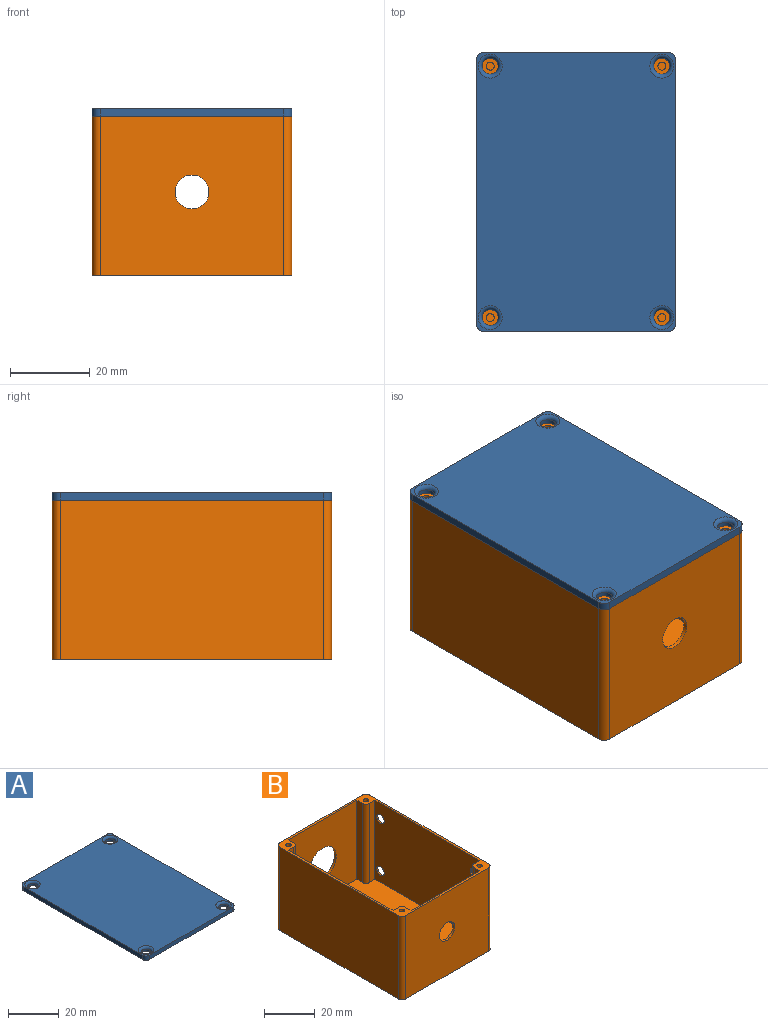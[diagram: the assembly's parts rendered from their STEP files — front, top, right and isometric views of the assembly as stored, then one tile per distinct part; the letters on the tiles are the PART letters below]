
ASSEMBLY  parts=2 mates=1
PART A: 18 faces, bbox 50x70x2 mm
  f0: plane 66x2mm, normal (-1,0,0), area 132mm2, adj f4,f5,f14,f17
  f1: plane 46x2mm, normal (0,-1,0), area 92mm2, adj f4,f5,f14,f15
  f2: plane 66x2mm, normal (1,0,0), area 132mm2, adj f4,f5,f15,f16
  f3: plane 46x2mm, normal (0,1,0), area 92mm2, adj f4,f5,f16,f17
  f4: plane 70x50mm, normal (0,0,1), area 3383.5mm2, adj f0,f1,f2,f3,f10,f11,f12,f13
  f5: plane 70x50mm, normal (0,0,-1), area 3446.3mm2, adj f0,f1,f2,f3,f6,f7,f8,f9
  f6: cylinder r=2mm len=4mm, axis (0,0,1), area 12.6mm2, adj f5,f13
  f7: cylinder r=2mm len=4mm, axis (0,0,1), area 12.6mm2, adj f5,f12
  f8: cylinder r=2mm len=4mm, axis (0,0,1), area 12.6mm2, adj f5,f11
  f9: cylinder r=2mm len=4mm, axis (0,0,1), area 12.6mm2, adj f5,f10
  f10: torus R=3mm, axis (0,0,1), area 23.3mm2, adj f4,f9
  f11: torus R=3mm, axis (0,0,1), area 23.3mm2, adj f4,f8
  f12: torus R=3mm, axis (0,0,1), area 23.3mm2, adj f4,f7
  f13: torus R=3mm, axis (0,0,1), area 23.3mm2, adj f4,f6
  f14: cylinder r=2mm len=2mm, axis (0,0,-1), area 6.3mm2, adj f0,f1,f4,f5
  f15: cylinder r=2mm len=2mm, axis (0,0,1), area 6.3mm2, adj f1,f2,f4,f5
  f16: cylinder r=2mm len=2mm, axis (0,0,-1), area 6.3mm2, adj f2,f3,f4,f5
  f17: cylinder r=2mm len=2mm, axis (0,0,1), area 6.3mm2, adj f0,f3,f4,f5
PART B: 42 faces, bbox 50x70x40 mm
  f0: plane 68x48mm, normal (0,0,1), area 3167.4mm2, adj f1,f2,f3,f4,f11,f12,f13,f14
  f1: plane 58x38mm, normal (-1,0,0), area 2146.2mm2, adj f0,f9,f16,f18,f35,f36,f37,f38
  f2: plane 38x38mm, normal (0,1,0), area 1387.3mm2, adj f0,f9,f13,f15,f40
  f3: plane 58x38mm, normal (1,0,0), area 2204mm2, adj f0,f9,f12,f14
  f4: plane 38x38mm, normal (0,-1,0), area 1267.3mm2, adj f0,f9,f11,f17,f41
  f5: plane 66x40mm, normal (-1,0,0), area 2640mm2, adj f9,f10,f31,f34
  f6: plane 46x40mm, normal (0,-1,0), area 1783.3mm2, adj f9,f10,f31,f32,f40
  f7: plane 66x40mm, normal (1,0,0), area 2558.3mm2, adj f9,f10,f32,f33,f35,f36,f37,f38
  f8: plane 46x40mm, normal (0,1,0), area 1663.3mm2, adj f9,f10,f33,f34,f41
  f9: plane 70x50mm, normal (0,0,1), area 316.6mm2, adj f1,f2,f3,f4,f5,f6,f7,f8
  f10: plane 70x50mm, normal (0,0,-1), area 3496.6mm2, adj f5,f6,f7,f8,f31,f32,f33,f34
  f11: plane 38x3mm, normal (1,0,0), area 114mm2, adj f0,f4,f9,f30
  f12: plane 38x3mm, normal (0,-1,0), area 114mm2, adj f0,f3,f9,f30
  f13: plane 38x3mm, normal (1,0,0), area 114mm2, adj f0,f2,f9,f27
  f14: plane 38x3mm, normal (0,1,0), area 114mm2, adj f0,f3,f9,f27
  f15: plane 38x3mm, normal (-1,0,0), area 114mm2, adj f0,f2,f9,f28
  f16: plane 38x3mm, normal (0,1,0), area 114mm2, adj f0,f1,f9,f28
  f17: plane 38x3mm, normal (-1,0,0), area 114mm2, adj f0,f4,f9,f29
  f18: plane 38x3mm, normal (0,-1,0), area 114mm2, adj f0,f1,f9,f29
  f19: cylinder r=1mm len=15mm, axis (0,0,1), area 94.2mm2, adj f9,f20
  f20: plane 2x2mm, normal (0,0,1), area 3.1mm2, adj f19
  f21: cylinder r=1mm len=15mm, axis (0,0,1), area 94.2mm2, adj f9,f22
  f22: plane 2x2mm, normal (0,0,1), area 3.1mm2, adj f21
  f23: cylinder r=1mm len=15mm, axis (0,0,1), area 94.2mm2, adj f9,f24
  f24: plane 2x2mm, normal (0,0,1), area 3.1mm2, adj f23
  f25: cylinder r=1mm len=15mm, axis (0,0,1), area 94.2mm2, adj f9,f26
  f26: plane 2x2mm, normal (0,0,1), area 3.1mm2, adj f25
  f27: cylinder r=2mm len=38mm, axis (0,0,1), area 119.4mm2, adj f0,f9,f13,f14
  f28: cylinder r=2mm len=38mm, axis (0,0,1), area 119.4mm2, adj f0,f9,f15,f16
  f29: cylinder r=2mm len=38mm, axis (0,0,1), area 119.4mm2, adj f0,f9,f17,f18
  f30: cylinder r=2mm len=38mm, axis (0,0,1), area 119.4mm2, adj f0,f9,f11,f12
  f31: cylinder r=2mm len=40mm, axis (0,0,-1), area 125.7mm2, adj f5,f6,f9,f10
  f32: cylinder r=2mm len=40mm, axis (0,0,1), area 125.7mm2, adj f6,f7,f9,f10
  f33: cylinder r=2mm len=40mm, axis (0,0,-1), area 125.7mm2, adj f7,f8,f9,f10
  f34: cylinder r=2mm len=40mm, axis (0,0,1), area 125.7mm2, adj f5,f8,f9,f10
  f35: cone r=2mm half-angle=22.5deg, axis (1,0,0), area 15.6mm2, adj f1,f7
  f36: cone r=2mm half-angle=22.5deg, axis (1,0,0), area 15.6mm2, adj f1,f7
  f37: cone r=2mm half-angle=22.5deg, axis (1,0,0), area 15.6mm2, adj f1,f7
  f38: cone r=2mm half-angle=22.5deg, axis (1,0,0), area 15.6mm2, adj f1,f7
  f39: cylinder r=1mm len=2mm, axis (1,0,0), area 6.3mm2, adj f1,f7
  f40: cylinder r=4.25mm len=8.5mm, axis (0,-1,0), area 26.7mm2, adj f2,f6
  f41: cylinder r=7.5mm len=15mm, axis (0,1,0), area 47.1mm2, adj f4,f8
PLACE A t=(-6.07,68.27,18.8)mm
PLACE B t=(-6.11,-5.83,-21.2)mm fixed
MATE slider B.f25 <-> A.f9  axis (0,0,1) through (12.1,15.3,18.8)mm
